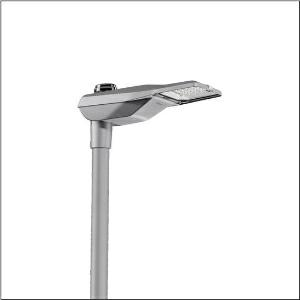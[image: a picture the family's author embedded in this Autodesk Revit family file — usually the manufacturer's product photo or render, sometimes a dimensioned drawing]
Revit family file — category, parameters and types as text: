
# Revit family: streetlight_sl_21_micro___stw1_0a_5xe5e47n08db_5020
name_source: partatom
category: Lighting Fixtures
units: mm (PartAtom-declared; Revit-internal decimal feet)

## family parameters
Cut with Voids When Loaded = No
Host = Face
Light Source = No
Part Type = Normal
Room Calculation Point = No
Round Connector Dimension = Use Diameter
Shared = No

## types (1)
- --- (1 x LED, 5320 lm, 39.1 W, 4000K)
    Apparent Load = 39 VA
    CIE Flux Codes = 38 75 98 100 100
    Color Rendering = 70
    Color Temperature = 4000K
    Default Elevation = 1800 mm
    Description = Streetlight SL 21 micro, mast luminaire, primary light control with lens, of PMMA, primary optical cover: cover, of toughened safety glass, transparent, light distribution: STW1.0a, light emission: direct distribution, primary light characteristic: asymmetric, installation type: post-top, LED, 3G 1.5mm², High Power LED, rated luminous flux: 5.320lm, luminous efficacy: 136lm/W, light colour: 740, colour temperature: 4000K, control: overheat protection, presetting dimming linear, constant luminous flux control, time-dependent luminous flux control, flexible luminous flux parameterisation, mains connection: 230..240V, AC, 50/60Hz, connection cable pre-assembled, cable length: 6,5m, wiring characteristics: H07RN-F, start of lifetime: 39W, end of service life: 41W, reduction: 18W, luminaire housing, of diecast aluminium (EN AC-44300), powder-coated, Siteco® metallic grey (DB 702S), corrosivity category C5 mid according to DIN EN ISO 12944, multi-level sealing system, sealing non-destructively replaceable, inclination adjustable: 0°, 5°, 10°, 15°, length: 528mm, width: 235mm, height: 110mm, spigot size: 76/60mm (post-top), protection rating (complete): IP66, insulation class (complete): insulation class I (protective earthing), certification: CE, ENEC, ENEC+, VDE, impact resistance: IK09, permissible operating ambient temperature for outdoor applications: -40..+50°C, standard-compliant lighting for roads and squares, packaging unit: 1 piece

Light Distribution: STW1.0a
    Height = 110 mm
    Lamp = 1 x LED
    Lamp Light Flux = 5320 lm
    Lamp Power = 39.1 W
    Lamp count = 1
    Length = 528 mm
    Luminous efficacy = 136 lm/W
    Manufacturer = Siteco
    ModVariant = No
    Model = 5XE5E47N08DB
    Number of Poles = 1
    OnlyDefault = Yes
    Power Factor = 1
    Product Name = Streetlight SL 21 micro | STW1.0a
    Product group = mast luminaire | pylon top
    ProductGroupID = 6100
    Protection Class = Protection class I
    Protection Degree = IP 66
    RLX_Detail_Level = 1
    RLX_Emergency_Light_Flux = 0 lm
    RLX_Emergency_Type = 0
    RLX_Emergency_Type_DB = No
    RlxData = <blob elided: 99225 chars, md5=229d6ce6>
    Socket = socket
    Standby Power = 0 W
    System Light Flux = 5320 lm
    System Power = 39 W
    Type Comments = factory setting: luminous flux: 100 % | dim-lin: 254 | 765 mA
    Type Image = l_1294375.jpg
    URL = http://relux.com
    VarID = @adj_085131
    Voltage = 0 V
    Weight = 0.00 kg
    Width = 235 mm

## geometry (parser evidence)
native form markers: Blend x4, Sweep x12
no freeform markers — native parametric forms only
